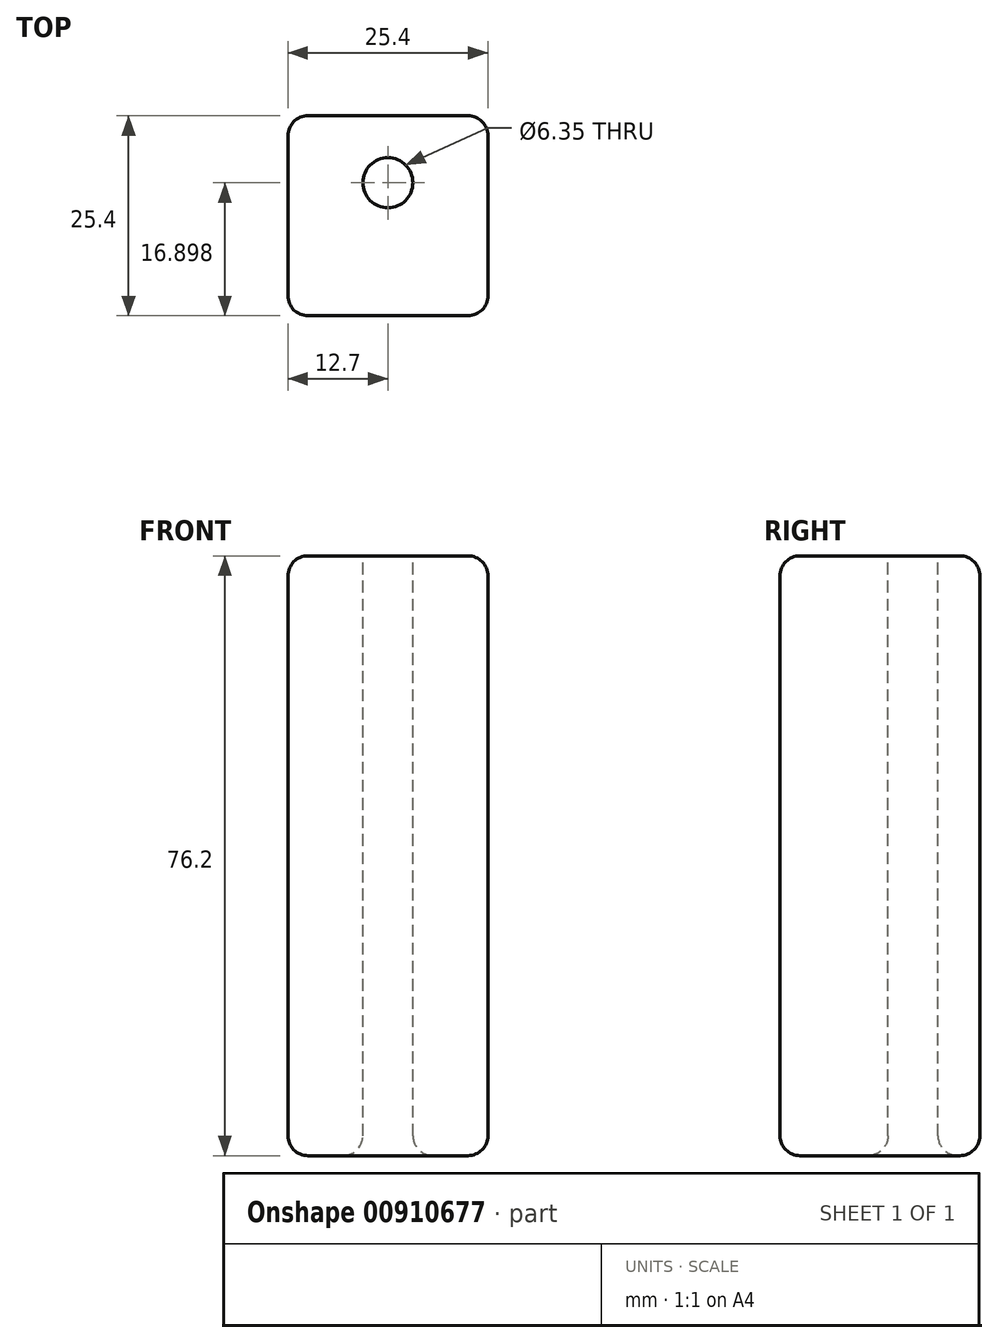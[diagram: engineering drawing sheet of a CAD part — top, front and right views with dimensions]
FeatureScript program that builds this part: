
annotation { "Feature Type Name" : "Feature", "Feature Type Description" : "" }
export const myFeature = defineFeature(function(context is Context, id is Id, definition is map)
    precondition{}
    {
        {
            var Q0;
            Q0=qCreatedBy(makeId("Front.planeOp"),FACE);
            var sketch = newSketch(context, id + "F0", { "sketchPlane" : qUnion([Q0])});
            skLineSegment(sketch, "E0.bottom", {"start": v(12.7, 38.1) * mm, "end": v(-12.7, 38.1) * mm});
            skLineSegment(sketch, "E0.top", {"start": v(12.7, -38.1) * mm, "end": v(-12.7, -38.1) * mm});
            skLineSegment(sketch, "E0.left", {"start": v(12.7, 38.1) * mm, "end": v(12.7, -38.1) * mm});
            skLineSegment(sketch, "E0.right", {"start": v(-12.7, 38.1) * mm, "end": v(-12.7, -38.1) * mm});
            skPoint(sketch, "E0.middle", {"position": v(0, 0) * mm});
            skSolve(sketch);
        }
        {
            var Q0;
            Q0=makeQuery(id+"F0.imprint","IMPRINT",FACE,{"disambiguationData":[TD([[makeQuery(id+"F0.imprint","IMPRINT",EDGE,{"derivedFrom":sQuery(id+"F0.wireOp",EDGE,"E0.bottom")}),1.0]])]});
            extrude(context, id + "F1", {"entities" : qUnion([Q0]), "depth" : 25.4 * mm, "offsetDistance" : 25.4 * mm});
        }
        {
            var Q0;
            Q0=makeQuery(id+"F1.opExtrude","SWEPT_FACE",FACE,{"disambiguationData":[OSD([sQuery(id+"F0.wireOp",EDGE,"E0.bottom")])]});
            var sketch = newSketch(context, id + "F2", { "sketchPlane" : qUnion([Q0])});
            skCircle(sketch, "E1", {"center": v(0, -8.5) * mm, "radius": 3.18 * mm});
            skSolve(sketch);
        }
        {
            var Q0;
            Q0 = qSketchRegion(id + "F2", true);
            var sketch = newSketch(context, id + "F3", { "sketchPlane" : qUnion([Q0])});
            skSolve(sketch);
        }
        {
            var Q0;
            Q0=makeQuery(id+"F3.imprint","IMPRINT",FACE,{"disambiguationData":[TD([[makeQuery(id+"F3.imprint","IMPRINT",EDGE,{"derivedFrom":makeQuery(id+"F2.imprint","IMPRINT",EDGE,{"derivedFrom":sQuery(id+"F2.wireOp",EDGE,"E1")})}),1.0]])]});
            extrude(context, id + "F4", {"entities" : qUnion([Q0]), "operationType" : NewBodyOperationType.REMOVE, "endBound" : BoundingType.THROUGH_ALL, "oppositeDirection" : true, "depth" : 25.4 * mm, "offsetDistance" : 25.4 * mm});
        }
        {
            var Q0;
            Q0=makeQuery(id+"F1.opExtrude","SWEPT_EDGE",EDGE,{"disambiguationData":[OSD([sQuery(id+"F0.wireOp",EDGE,"E0.bottom"),sQuery(id+"F0.wireOp",EDGE,"E0.left")])]});
            var Q1;
            Q1=makeQuery(id+"F1.opExtrude","CAP_EDGE",EDGE,{"disambiguationData":[OSD([sQuery(id+"F0.wireOp",EDGE,"E0.bottom")])],"isStart":false});
            var Q2;
            Q2=makeQuery(id+"F1.opExtrude","SWEPT_EDGE",EDGE,{"disambiguationData":[OSD([sQuery(id+"F0.wireOp",EDGE,"E0.bottom"),sQuery(id+"F0.wireOp",EDGE,"E0.right")])]});
            var Q3;
            Q3=makeQuery(id+"F1.opExtrude","CAP_EDGE",EDGE,{"disambiguationData":[OSD([sQuery(id+"F0.wireOp",EDGE,"E0.left")])],"isStart":false});
            var Q4;
            Q4=makeQuery(id+"F1.opExtrude","CAP_EDGE",EDGE,{"disambiguationData":[OSD([sQuery(id+"F0.wireOp",EDGE,"E0.right")])],"isStart":false});
            var Q5;
            Q5=makeQuery(id+"F1.opExtrude","CAP_EDGE",EDGE,{"disambiguationData":[OSD([sQuery(id+"F0.wireOp",EDGE,"E0.right")])],"isStart":true});
            var Q6;
            Q6=makeQuery(id+"F4.boolean.opBoolean","INTERSECT",EDGE,{"derivedFrom":[makeQuery(id+"F1.opExtrude","SWEPT_FACE",FACE,{"disambiguationData":[OSD([sQuery(id+"F0.wireOp",EDGE,"E0.top")])]}),makeQuery(id+"F4.opExtrude","SWEPT_FACE",FACE,{"disambiguationData":[OSD([sQuery(id+"F2.wireOp",EDGE,"E1")])]})]});
            var Q7;
            Q7=makeQuery(id+"F4.boolean.opBoolean","COPY",EDGE,{"derivedFrom":makeQuery(id+"F4.opExtrude","CAP_EDGE",EDGE,{"disambiguationData":[OSD([sQuery(id+"F2.wireOp",EDGE,"E1")])],"isStart":true})});
            var Q8;
            Q8=makeQuery(id+"F1.opExtrude","CAP_EDGE",EDGE,{"disambiguationData":[OSD([sQuery(id+"F0.wireOp",EDGE,"E0.bottom")])],"isStart":true});
            var Q9;
            Q9=makeQuery(id+"F1.opExtrude","CAP_EDGE",EDGE,{"disambiguationData":[OSD([sQuery(id+"F0.wireOp",EDGE,"E0.left")])],"isStart":true});
            var Q10;
            Q10=makeQuery(id+"F1.opExtrude","CAP_EDGE",EDGE,{"disambiguationData":[OSD([sQuery(id+"F0.wireOp",EDGE,"E0.top")])],"isStart":true});
            var Q11;
            Q11=makeQuery(id+"F1.opExtrude","SWEPT_EDGE",EDGE,{"disambiguationData":[OSD([sQuery(id+"F0.wireOp",EDGE,"E0.top"),sQuery(id+"F0.wireOp",EDGE,"E0.left")])]});
            var Q12;
            Q12=makeQuery(id+"F1.opExtrude","CAP_EDGE",EDGE,{"disambiguationData":[OSD([sQuery(id+"F0.wireOp",EDGE,"E0.top")])],"isStart":false});
            var Q13;
            Q13=makeQuery(id+"F1.opExtrude","SWEPT_EDGE",EDGE,{"disambiguationData":[OSD([sQuery(id+"F0.wireOp",EDGE,"E0.top"),sQuery(id+"F0.wireOp",EDGE,"E0.right")])]});
            fillet(context, id + "F5", {"entities" : qUnion([Q0, Q1, Q2, Q3, Q4, Q5, Q6, Q7, Q8, Q9, Q10, Q11, Q12, Q13]), "radius" : 2.54 * mm, "tangentPropagation" : true, "allowEdgeOverflow" : false});
        }
    });
